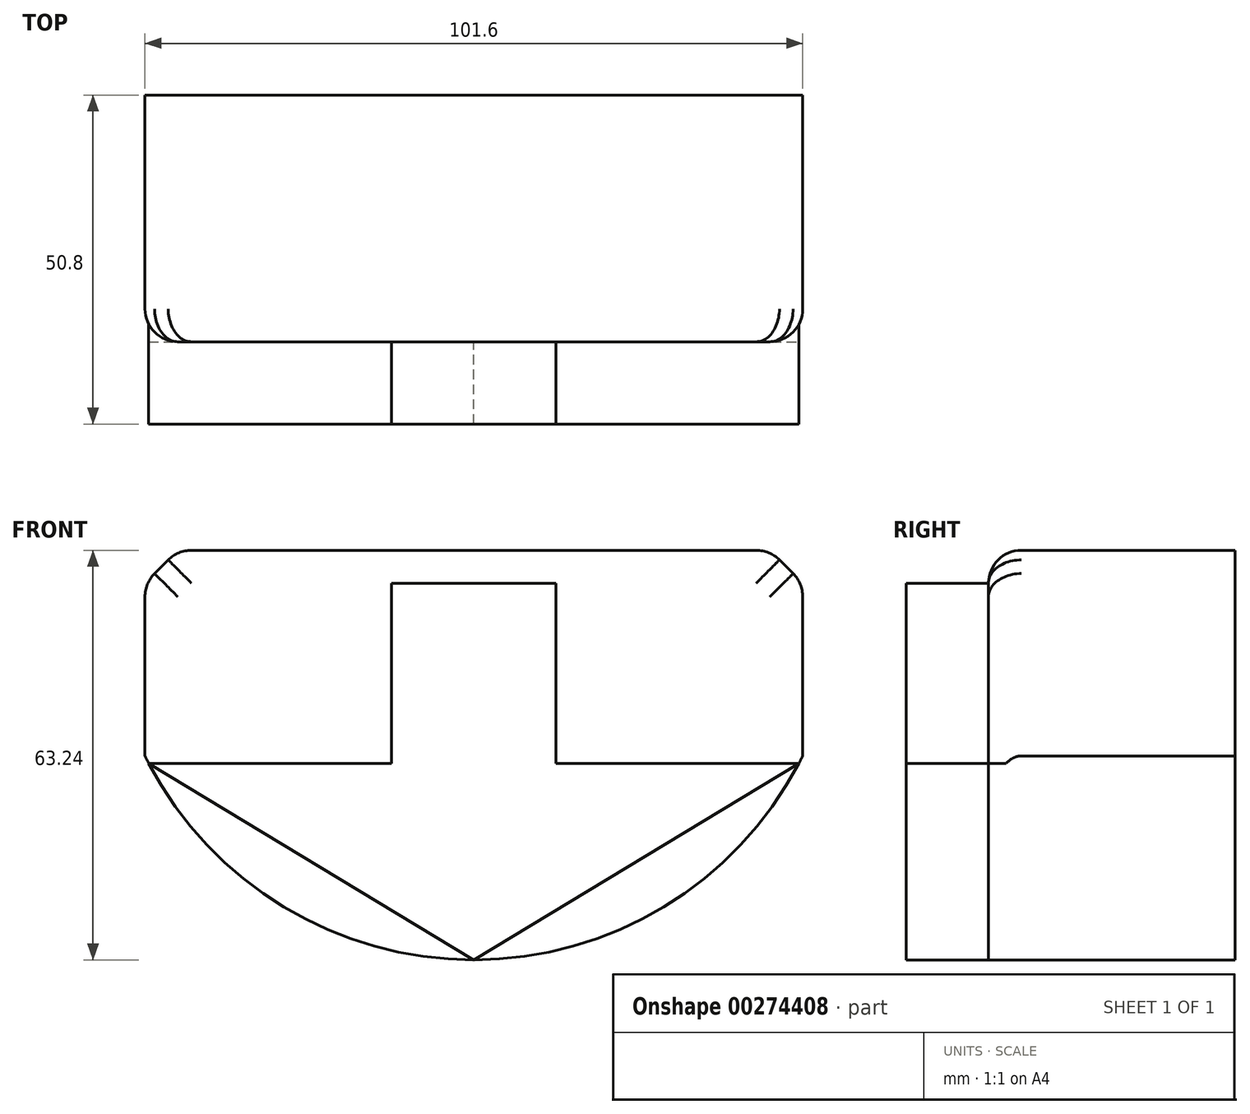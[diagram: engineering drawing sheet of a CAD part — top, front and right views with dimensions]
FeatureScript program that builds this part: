
annotation { "Feature Type Name" : "Feature", "Feature Type Description" : "" }
export const myFeature = defineFeature(function(context is Context, id is Id, definition is map)
    precondition{}
    {
        {
            var Q0;
            Q0=qCreatedBy(makeId("Front.planeOp"),FACE);
            var sketch = newSketch(context, id + "F0", { "sketchPlane" : qUnion([Q0])});
            skLineSegment(sketch, "E0", {"start": v(-36.23, 36.17) * mm, "end": v(-36.23, -27.33) * mm});
            skLineSegment(sketch, "E1", {"start": v(-36.23, -27.33) * mm, "end": v(65.37, -27.33) * mm});
            skLineSegment(sketch, "E2", {"start": v(65.37, -27.33) * mm, "end": v(65.37, 36.17) * mm});
            skLineSegment(sketch, "E3", {"start": v(65.37, 36.17) * mm, "end": v(-36.23, 36.17) * mm});
            skSolve(sketch);
        }
        {
            var Q0;
            Q0 = qSketchRegion(id + "F0", true);
            extrude(context, id + "F1", {"entities" : qUnion([Q0]), "depth" : 38.1 * mm});
        }
        {
            var Q0;
            Q0=makeQuery(id+"F1.opExtrude","CAP_FACE",FACE,{"disambiguationData":[OSD([sQuery(id+"F0.wireOp",EDGE,"E0"),sQuery(id+"F0.wireOp",EDGE,"E1"),sQuery(id+"F0.wireOp",EDGE,"E2"),sQuery(id+"F0.wireOp",EDGE,"E3")])],"isStart":false});
            var sketch = newSketch(context, id + "F2", { "sketchPlane" : qUnion([Q0])});
            skArc(sketch, "E4", {"start": v(-36.23, 4.42) * mm, "mid": v(14.57, -27.07) * mm, "end": v(65.37, 4.42) * mm});
            skSolve(sketch);
        }
        {
            var Q0;
            Q0 = qSketchRegion(id + "F2", true);
            var Q1;
            {var subQ0=sQuery(id+"F2.wireOp",EDGE,"E4");Q1=makeQuery(id+"F2.imprint","IMPRINT",FACE,{"disambiguationData":[TD([[makeQuery(id+"F2.imprint","IMPRINT",EDGE,{"derivedFrom":subQ0}),-1.0]])]});}
            extrude(context, id + "F3", {"entities" : qUnion([Q0, Q1]), "operationType" : NewBodyOperationType.REMOVE, "oppositeDirection" : true, "depth" : 48 * mm});
        }
        {
            var Q0;
            Q0=makeQuery(id+"F1.opExtrude","SWEPT_EDGE",EDGE,{"disambiguationData":[OSD([sQuery(id+"F0.wireOp",EDGE,"E0"),sQuery(id+"F0.wireOp",EDGE,"E3")])]});
            var Q1;
            Q1=makeQuery(id+"F1.opExtrude","SWEPT_EDGE",EDGE,{"disambiguationData":[OSD([sQuery(id+"F0.wireOp",EDGE,"E2"),sQuery(id+"F0.wireOp",EDGE,"E3")])]});
            var Q2;
            Q2=makeQuery(id+"F3.boolean.opBoolean","COPY",EDGE,{"derivedFrom":makeQuery(id+"F3.opExtrude","SWEPT_EDGE",EDGE,{"disambiguationData":[OSD([sQuery(id+"F0.wireOp",EDGE,"E2"),sQuery(id+"F2.wireOp",EDGE,"E4")])]})});
            var Q3;
            Q3=makeQuery(id+"F3.boolean.opBoolean","COPY",EDGE,{"derivedFrom":makeQuery(id+"F3.opExtrude","SWEPT_EDGE",EDGE,{"disambiguationData":[OSD([sQuery(id+"F0.wireOp",EDGE,"E0"),sQuery(id+"F2.wireOp",EDGE,"E4")])]})});
            chamfer(context, id + "F4", {"entities" : qUnion([Q0, Q1, Q2, Q3]), "width" : 5.08 * mm, "tangentPropagation" : true});
        }
        {
            var Q0;
            Q0=makeQuery(id+"F1.opExtrude","CAP_FACE",FACE,{"disambiguationData":[OSD([sQuery(id+"F0.wireOp",EDGE,"E0"),sQuery(id+"F0.wireOp",EDGE,"E1"),sQuery(id+"F0.wireOp",EDGE,"E2"),sQuery(id+"F0.wireOp",EDGE,"E3")])],"isStart":false});
            var sketch = newSketch(context, id + "F5", { "sketchPlane" : qUnion([Q0])});
            skLineSegment(sketch, "E5", {"start": v(-35.65, 3.28) * mm, "end": v(64.79, 3.28) * mm});
            skLineSegment(sketch, "E6", {"start": v(64.79, 3.28) * mm, "end": v(14.57, -27.07) * mm});
            skLineSegment(sketch, "E7", {"start": v(14.57, -27.07) * mm, "end": v(-35.65, 3.28) * mm});
            skSolve(sketch);
        }
        {
            var Q0;
            Q0 = qSketchRegion(id + "F5", true);
            extrude(context, id + "F6", {"entities" : qUnion([Q0]), "operationType" : NewBodyOperationType.ADD, "depth" : 12.7 * mm});
        }
        {
            var Q0;
            {var subQ0=sQuery(id+"F2.wireOp",EDGE,"E4");var subQ1=sQuery(id+"F0.wireOp",EDGE,"E0");Q0=makeQuery(id+"F6.boolean.opBoolean","SPLIT",EDGE,{"disambiguationData":[TD([makeQuery(id+"F4.opChamfer","BLEND_FACE",FACE,{"disambiguationData":[OSD([subQ1,subQ0])]})])],"derivedFrom":makeQuery(id+"F3.boolean.opBoolean","COPY",EDGE,{"derivedFrom":makeQuery(id+"F3.opExtrude","CAP_EDGE",EDGE,{"disambiguationData":[OSD([subQ0])],"isStart":true})})});}
            var Q1;
            {var subQ0=sQuery(id+"F2.wireOp",EDGE,"E4");var subQ1=sQuery(id+"F0.wireOp",EDGE,"E2");Q1=makeQuery(id+"F6.boolean.opBoolean","SPLIT",EDGE,{"disambiguationData":[TD([makeQuery(id+"F4.opChamfer","BLEND_FACE",FACE,{"disambiguationData":[OSD([subQ1,subQ0])]})])],"derivedFrom":makeQuery(id+"F3.boolean.opBoolean","COPY",EDGE,{"derivedFrom":makeQuery(id+"F3.opExtrude","CAP_EDGE",EDGE,{"disambiguationData":[OSD([subQ0])],"isStart":true})})});}
            var Q2;
            Q2=makeQuery(id+"F1.opExtrude","CAP_EDGE",EDGE,{"disambiguationData":[OSD([sQuery(id+"F0.wireOp",EDGE,"E0")])],"isStart":false});
            var Q3;
            {var subQ0=sQuery(id+"F0.wireOp",EDGE,"E0");Q3=makeQuery(id+"F4.opChamfer","BLEND_EDGE",EDGE,{"blendedFrom":[makeQuery(id+"F3.boolean.opBoolean","COPY",EDGE,{"derivedFrom":makeQuery(id+"F3.opExtrude","SWEPT_EDGE",EDGE,{"disambiguationData":[OSD([subQ0,sQuery(id+"F2.wireOp",EDGE,"E4")])]})}),makeQuery(id+"F1.opExtrude","CAP_FACE",FACE,{"disambiguationData":[OSD([subQ0,sQuery(id+"F0.wireOp",EDGE,"E1"),sQuery(id+"F0.wireOp",EDGE,"E2"),sQuery(id+"F0.wireOp",EDGE,"E3")])],"isStart":false})],"blendedInto":[makeQuery(id+"F1.opExtrude","CAP_FACE",FACE,{"disambiguationData":[OSD([subQ0,sQuery(id+"F0.wireOp",EDGE,"E1"),sQuery(id+"F0.wireOp",EDGE,"E2"),sQuery(id+"F0.wireOp",EDGE,"E3")])],"isStart":false})]});}
            var Q4;
            {var subQ0=sQuery(id+"F0.wireOp",EDGE,"E3");var subQ1=sQuery(id+"F0.wireOp",EDGE,"E0");Q4=makeQuery(id+"F4.opChamfer","BLEND_EDGE",EDGE,{"blendedFrom":[makeQuery(id+"F1.opExtrude","SWEPT_EDGE",EDGE,{"disambiguationData":[OSD([subQ1,subQ0])]}),makeQuery(id+"F1.opExtrude","CAP_FACE",FACE,{"disambiguationData":[OSD([subQ1,sQuery(id+"F0.wireOp",EDGE,"E1"),sQuery(id+"F0.wireOp",EDGE,"E2"),subQ0])],"isStart":false})],"blendedInto":[makeQuery(id+"F1.opExtrude","CAP_FACE",FACE,{"disambiguationData":[OSD([subQ1,sQuery(id+"F0.wireOp",EDGE,"E1"),sQuery(id+"F0.wireOp",EDGE,"E2"),subQ0])],"isStart":false})]});}
            var Q5;
            Q5=makeQuery(id+"F1.opExtrude","CAP_EDGE",EDGE,{"disambiguationData":[OSD([sQuery(id+"F0.wireOp",EDGE,"E3")])],"isStart":false});
            var Q6;
            {var subQ0=sQuery(id+"F0.wireOp",EDGE,"E2");Q6=makeQuery(id+"F4.opChamfer","BLEND_EDGE",EDGE,{"blendedFrom":[makeQuery(id+"F3.boolean.opBoolean","COPY",EDGE,{"derivedFrom":makeQuery(id+"F3.opExtrude","SWEPT_EDGE",EDGE,{"disambiguationData":[OSD([subQ0,sQuery(id+"F2.wireOp",EDGE,"E4")])]})}),makeQuery(id+"F1.opExtrude","CAP_FACE",FACE,{"disambiguationData":[OSD([sQuery(id+"F0.wireOp",EDGE,"E0"),sQuery(id+"F0.wireOp",EDGE,"E1"),subQ0,sQuery(id+"F0.wireOp",EDGE,"E3")])],"isStart":false})],"blendedInto":[makeQuery(id+"F1.opExtrude","CAP_FACE",FACE,{"disambiguationData":[OSD([sQuery(id+"F0.wireOp",EDGE,"E0"),sQuery(id+"F0.wireOp",EDGE,"E1"),subQ0,sQuery(id+"F0.wireOp",EDGE,"E3")])],"isStart":false})]});}
            var Q7;
            Q7=makeQuery(id+"F1.opExtrude","CAP_EDGE",EDGE,{"disambiguationData":[OSD([sQuery(id+"F0.wireOp",EDGE,"E2")])],"isStart":false});
            var Q8;
            {var subQ0=sQuery(id+"F0.wireOp",EDGE,"E3");var subQ1=sQuery(id+"F0.wireOp",EDGE,"E2");Q8=makeQuery(id+"F4.opChamfer","BLEND_EDGE",EDGE,{"blendedFrom":[makeQuery(id+"F1.opExtrude","SWEPT_EDGE",EDGE,{"disambiguationData":[OSD([subQ1,subQ0])]}),makeQuery(id+"F1.opExtrude","CAP_FACE",FACE,{"disambiguationData":[OSD([sQuery(id+"F0.wireOp",EDGE,"E0"),sQuery(id+"F0.wireOp",EDGE,"E1"),subQ1,subQ0])],"isStart":false})],"blendedInto":[makeQuery(id+"F1.opExtrude","CAP_FACE",FACE,{"disambiguationData":[OSD([sQuery(id+"F0.wireOp",EDGE,"E0"),sQuery(id+"F0.wireOp",EDGE,"E1"),subQ1,subQ0])],"isStart":false})]});}
            fillet(context, id + "F7", {"entities" : qUnion([Q0, Q1, Q2, Q3, Q4, Q5, Q6, Q7, Q8]), "radius" : 5.08 * mm, "tangentPropagation" : true, "allowEdgeOverflow" : false});
        }
        {
            var Q0;
            {var subQ0=sQuery(id+"F0.wireOp",EDGE,"E0");var subQ1=sQuery(id+"F0.wireOp",EDGE,"E3");Q0=makeQuery(id+"F7.opFillet","BLEND_EDGE",EDGE,{"blendedFrom":[makeQuery(id+"F4.opChamfer","BLEND_EDGE",EDGE,{"blendedFrom":[makeQuery(id+"F1.opExtrude","SWEPT_EDGE",EDGE,{"disambiguationData":[OSD([subQ0,subQ1])]}),makeQuery(id+"F1.opExtrude","CAP_FACE",FACE,{"disambiguationData":[OSD([subQ0,sQuery(id+"F0.wireOp",EDGE,"E1"),sQuery(id+"F0.wireOp",EDGE,"E2"),subQ1])],"isStart":false})],"blendedInto":[makeQuery(id+"F1.opExtrude","CAP_FACE",FACE,{"disambiguationData":[OSD([subQ0,sQuery(id+"F0.wireOp",EDGE,"E1"),sQuery(id+"F0.wireOp",EDGE,"E2"),subQ1])],"isStart":false})]}),makeQuery(id+"F1.opExtrude","CAP_EDGE",EDGE,{"disambiguationData":[OSD([subQ0])],"isStart":false})],"blendedInto":[]});}
            var Q1;
            {var subQ0=sQuery(id+"F0.wireOp",EDGE,"E3");var subQ1=sQuery(id+"F0.wireOp",EDGE,"E0");Q1=makeQuery(id+"F7.opFillet","BLEND_EDGE",EDGE,{"blendedFrom":[makeQuery(id+"F4.opChamfer","BLEND_EDGE",EDGE,{"blendedFrom":[makeQuery(id+"F1.opExtrude","SWEPT_EDGE",EDGE,{"disambiguationData":[OSD([subQ1,subQ0])]}),makeQuery(id+"F1.opExtrude","CAP_FACE",FACE,{"disambiguationData":[OSD([subQ1,sQuery(id+"F0.wireOp",EDGE,"E1"),sQuery(id+"F0.wireOp",EDGE,"E2"),subQ0])],"isStart":false})],"blendedInto":[makeQuery(id+"F1.opExtrude","CAP_FACE",FACE,{"disambiguationData":[OSD([subQ1,sQuery(id+"F0.wireOp",EDGE,"E1"),sQuery(id+"F0.wireOp",EDGE,"E2"),subQ0])],"isStart":false})]}),makeQuery(id+"F1.opExtrude","CAP_EDGE",EDGE,{"disambiguationData":[OSD([subQ0])],"isStart":false})],"blendedInto":[]});}
            var Q2;
            {var subQ0=sQuery(id+"F0.wireOp",EDGE,"E0");Q2=makeQuery(id+"F7.opFillet","BLEND_EDGE",EDGE,{"blendedFrom":[makeQuery(id+"F4.opChamfer","BLEND_EDGE",EDGE,{"blendedFrom":[makeQuery(id+"F3.boolean.opBoolean","COPY",EDGE,{"derivedFrom":makeQuery(id+"F3.opExtrude","SWEPT_EDGE",EDGE,{"disambiguationData":[OSD([subQ0,sQuery(id+"F2.wireOp",EDGE,"E4")])]})}),makeQuery(id+"F1.opExtrude","CAP_FACE",FACE,{"disambiguationData":[OSD([subQ0,sQuery(id+"F0.wireOp",EDGE,"E1"),sQuery(id+"F0.wireOp",EDGE,"E2"),sQuery(id+"F0.wireOp",EDGE,"E3")])],"isStart":false})],"blendedInto":[makeQuery(id+"F1.opExtrude","CAP_FACE",FACE,{"disambiguationData":[OSD([subQ0,sQuery(id+"F0.wireOp",EDGE,"E1"),sQuery(id+"F0.wireOp",EDGE,"E2"),sQuery(id+"F0.wireOp",EDGE,"E3")])],"isStart":false})]}),makeQuery(id+"F1.opExtrude","CAP_EDGE",EDGE,{"disambiguationData":[OSD([subQ0])],"isStart":false})],"blendedInto":[]});}
            var Q3;
            {var subQ0=sQuery(id+"F0.wireOp",EDGE,"E2");var subQ1=sQuery(id+"F0.wireOp",EDGE,"E3");Q3=makeQuery(id+"F7.opFillet","BLEND_EDGE",EDGE,{"blendedFrom":[makeQuery(id+"F4.opChamfer","BLEND_EDGE",EDGE,{"blendedFrom":[makeQuery(id+"F1.opExtrude","SWEPT_EDGE",EDGE,{"disambiguationData":[OSD([subQ0,subQ1])]}),makeQuery(id+"F1.opExtrude","CAP_FACE",FACE,{"disambiguationData":[OSD([sQuery(id+"F0.wireOp",EDGE,"E0"),sQuery(id+"F0.wireOp",EDGE,"E1"),subQ0,subQ1])],"isStart":false})],"blendedInto":[makeQuery(id+"F1.opExtrude","CAP_FACE",FACE,{"disambiguationData":[OSD([sQuery(id+"F0.wireOp",EDGE,"E0"),sQuery(id+"F0.wireOp",EDGE,"E1"),subQ0,subQ1])],"isStart":false})]}),makeQuery(id+"F1.opExtrude","CAP_EDGE",EDGE,{"disambiguationData":[OSD([subQ0])],"isStart":false})],"blendedInto":[]});}
            var Q4;
            {var subQ0=sQuery(id+"F0.wireOp",EDGE,"E3");var subQ1=sQuery(id+"F0.wireOp",EDGE,"E2");Q4=makeQuery(id+"F7.opFillet","BLEND_EDGE",EDGE,{"blendedFrom":[makeQuery(id+"F4.opChamfer","BLEND_EDGE",EDGE,{"blendedFrom":[makeQuery(id+"F1.opExtrude","SWEPT_EDGE",EDGE,{"disambiguationData":[OSD([subQ1,subQ0])]}),makeQuery(id+"F1.opExtrude","CAP_FACE",FACE,{"disambiguationData":[OSD([sQuery(id+"F0.wireOp",EDGE,"E0"),sQuery(id+"F0.wireOp",EDGE,"E1"),subQ1,subQ0])],"isStart":false})],"blendedInto":[makeQuery(id+"F1.opExtrude","CAP_FACE",FACE,{"disambiguationData":[OSD([sQuery(id+"F0.wireOp",EDGE,"E0"),sQuery(id+"F0.wireOp",EDGE,"E1"),subQ1,subQ0])],"isStart":false})]}),makeQuery(id+"F1.opExtrude","CAP_EDGE",EDGE,{"disambiguationData":[OSD([subQ0])],"isStart":false})],"blendedInto":[]});}
            var Q5;
            {var subQ0=sQuery(id+"F0.wireOp",EDGE,"E2");Q5=makeQuery(id+"F7.opFillet","BLEND_EDGE",EDGE,{"blendedFrom":[makeQuery(id+"F4.opChamfer","BLEND_EDGE",EDGE,{"blendedFrom":[makeQuery(id+"F3.boolean.opBoolean","COPY",EDGE,{"derivedFrom":makeQuery(id+"F3.opExtrude","SWEPT_EDGE",EDGE,{"disambiguationData":[OSD([subQ0,sQuery(id+"F2.wireOp",EDGE,"E4")])]})}),makeQuery(id+"F1.opExtrude","CAP_FACE",FACE,{"disambiguationData":[OSD([sQuery(id+"F0.wireOp",EDGE,"E0"),sQuery(id+"F0.wireOp",EDGE,"E1"),subQ0,sQuery(id+"F0.wireOp",EDGE,"E3")])],"isStart":false})],"blendedInto":[makeQuery(id+"F1.opExtrude","CAP_FACE",FACE,{"disambiguationData":[OSD([sQuery(id+"F0.wireOp",EDGE,"E0"),sQuery(id+"F0.wireOp",EDGE,"E1"),subQ0,sQuery(id+"F0.wireOp",EDGE,"E3")])],"isStart":false})]}),makeQuery(id+"F1.opExtrude","CAP_EDGE",EDGE,{"disambiguationData":[OSD([subQ0])],"isStart":false})],"blendedInto":[]});}
            fillet(context, id + "F8", {"entities" : qUnion([Q0, Q1, Q2, Q3, Q4, Q5]), "radius" : 5.08 * mm, "tangentPropagation" : true, "allowEdgeOverflow" : false});
        }
        {
            var Q0;
            {var subQ0=sQuery(id+"F2.wireOp",EDGE,"E4");var subQ1=sQuery(id+"F0.wireOp",EDGE,"E2");var subQ2=sQuery(id+"F0.wireOp",EDGE,"E3");var subQ3=sQuery(id+"F0.wireOp",EDGE,"E0");var subQ4=makeQuery(id+"F1.opExtrude","CAP_FACE",FACE,{"disambiguationData":[OSD([subQ3,sQuery(id+"F0.wireOp",EDGE,"E1"),subQ1,subQ2])],"isStart":false});Q0=makeQuery(id+"F6.boolean.opBoolean","SPLIT",FACE,{"disambiguationData":[TD([makeQuery(id+"F1.opExtrude","SWEPT_FACE",FACE,{"disambiguationData":[OSD([subQ3])]}),subQ4,makeQuery(id+"F1.opExtrude","SWEPT_FACE",FACE,{"disambiguationData":[OSD([subQ1])]}),makeQuery(id+"F1.opExtrude","SWEPT_FACE",FACE,{"disambiguationData":[OSD([subQ2])]}),makeQuery(id+"F3.boolean.opBoolean","COPY",FACE,{"derivedFrom":makeQuery(id+"F3.opExtrude","SWEPT_FACE",FACE,{"disambiguationData":[OSD([subQ0])]})}),makeQuery(id+"F4.opChamfer","BLEND_FACE",FACE,{"disambiguationData":[OSD([subQ3,subQ2])]}),makeQuery(id+"F4.opChamfer","BLEND_FACE",FACE,{"disambiguationData":[OSD([subQ1,subQ2])]}),makeQuery(id+"F4.opChamfer","BLEND_FACE",FACE,{"disambiguationData":[OSD([subQ3,subQ0])]}),makeQuery(id+"F4.opChamfer","BLEND_FACE",FACE,{"disambiguationData":[OSD([subQ1,subQ0])]}),makeQuery(id+"F6.opExtrude","SWEPT_FACE",FACE,{"disambiguationData":[OSD([sQuery(id+"F5.wireOp",EDGE,"E5")])]}),makeQuery(id+"F6.opExtrude","SWEPT_FACE",FACE,{"disambiguationData":[OSD([sQuery(id+"F5.wireOp",EDGE,"E6")])]}),makeQuery(id+"F6.opExtrude","SWEPT_FACE",FACE,{"disambiguationData":[OSD([sQuery(id+"F5.wireOp",EDGE,"E7")])]})])],"derivedFrom":subQ4});}
            var sketch = newSketch(context, id + "F9", { "sketchPlane" : qUnion([Q0])});
            skLineSegment(sketch, "E8", {"start": v(14.57, 3.28) * mm, "end": v(14.57, 31.09) * mm});
            skLineSegment(sketch, "E9", {"start": v(14.57, 31.09) * mm, "end": v(27.27, 31.09) * mm});
            skLineSegment(sketch, "E10", {"start": v(27.27, 31.09) * mm, "end": v(27.27, 3.28) * mm});
            skLineSegment(sketch, "E11", {"start": v(27.27, 3.28) * mm, "end": v(14.57, 3.28) * mm});
            skLineSegment(sketch, "E12", {"start": v(14.57, 3.28) * mm, "end": v(1.87, 3.28) * mm});
            skLineSegment(sketch, "E13", {"start": v(1.87, 3.28) * mm, "end": v(1.87, 31.09) * mm});
            skLineSegment(sketch, "E14", {"start": v(1.87, 31.09) * mm, "end": v(14.57, 31.09) * mm});
            skSolve(sketch);
        }
        {
            var Q0;
            Q0 = qSketchRegion(id + "F9", true);
            extrude(context, id + "F10", {"entities" : qUnion([Q0]), "operationType" : NewBodyOperationType.ADD, "depth" : 12.7 * mm});
        }
    });
